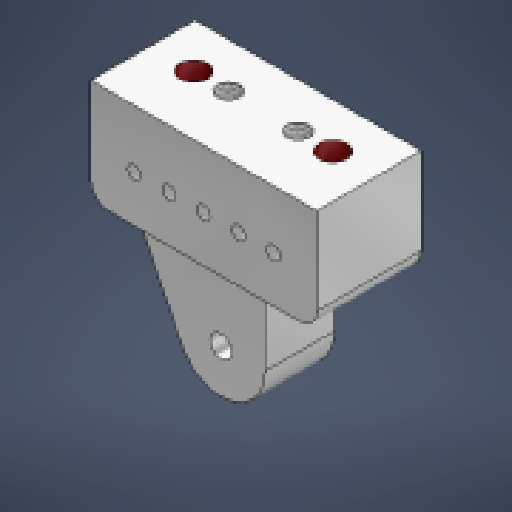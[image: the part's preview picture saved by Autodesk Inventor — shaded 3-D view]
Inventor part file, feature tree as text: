
AUTODESK INVENTOR PART (.ipt)
format: ipt  version: 2024.3 (Build 283343000, 343)  size: 327,680 bytes
history: native  units: mm (DEFAULTED — no unit token found)
features: sketch x6, hole x4, fillet x3, projected_geometry x3, extrude x2, pattern_linear x1
ambient origin geometry x8: Origin, YZ Plane, XZ Plane, XY Plane, X Axis, Y Axis, Z Axis, Center Point
bodies: Solid1 (feature_tree)
feature tree (19):
  extrude  "Extrusion1"  Depth=44.45mm
  fillet  "Fillet1"  Radius=19.05mm
  hole  "Hole1"  [1 undecoded]
  hole  "Hole2"  [1 undecoded]
  hole  "Hole3"  [1 undecoded]
  extrude  "Extrusion2"  Depth=25.4mm
  hole  "Hole4"  [1 undecoded]
  pattern_linear  "Rectangular Pattern1"  Spacing1=6.35mm  [1 undecoded]
  fillet  "Fillet3"  Radius=3.175mm
  fillet  "Fillet2"  Radius=3.175mm
  sketch  "Sketch2"  dims[d0=41.275mm d1=44.45mm d2=19.05mm d3=0.0mm]
  sketch  "Sketch3"  dims[d4=19.05mm d8=15.875mm]
  sketch  "Sketch4"  dims[d9=3.175mm d10=25.4mm]
  projected_geometry  "Projected Loop1"
  projected_geometry  "Projected Loop2"
  sketch  "Sketch5"  dims[d11=8.189483mm d12=7.9375mm]
  sketch  "Sketch6"  dims[d13=7.9375mm d14=25.4mm]
  projected_geometry  "Projected Loop3"
  sketch  "Sketch7"  dims[d15=5.0038mm d16=19.05mm d17=5.5118mm d18=5.7912mm d19=90.0deg d20=6.35mm d21=20.594885mm d22=6.35mm d23=3.9624mm d24=9.652mm d25=9.779mm d26=6.35mm d27=14.3117mm d28=13.6144mm d29=20.594885mm d30=3.9624mm d31=9.652mm d32=9.525mm d33=6.35mm d34=14.3117mm d35=13.6144mm d36=20.594885mm d37=6.35mm d38=0.0mm d39=3.175mm d40=3.175mm d43=10.6299mm d44=2.459mm d45=9.525mm d46=9.525mm d47=6.35mm d48=14.3117mm d49=12.7mm d50=20.594885mm d51=50.0mm d53=6.35mm]
note: 5 required parameter values undecoded (feature->parameter linkage not recoverable at this tier; creation-order binding heuristic only, values carry confidence <= 0.55)
